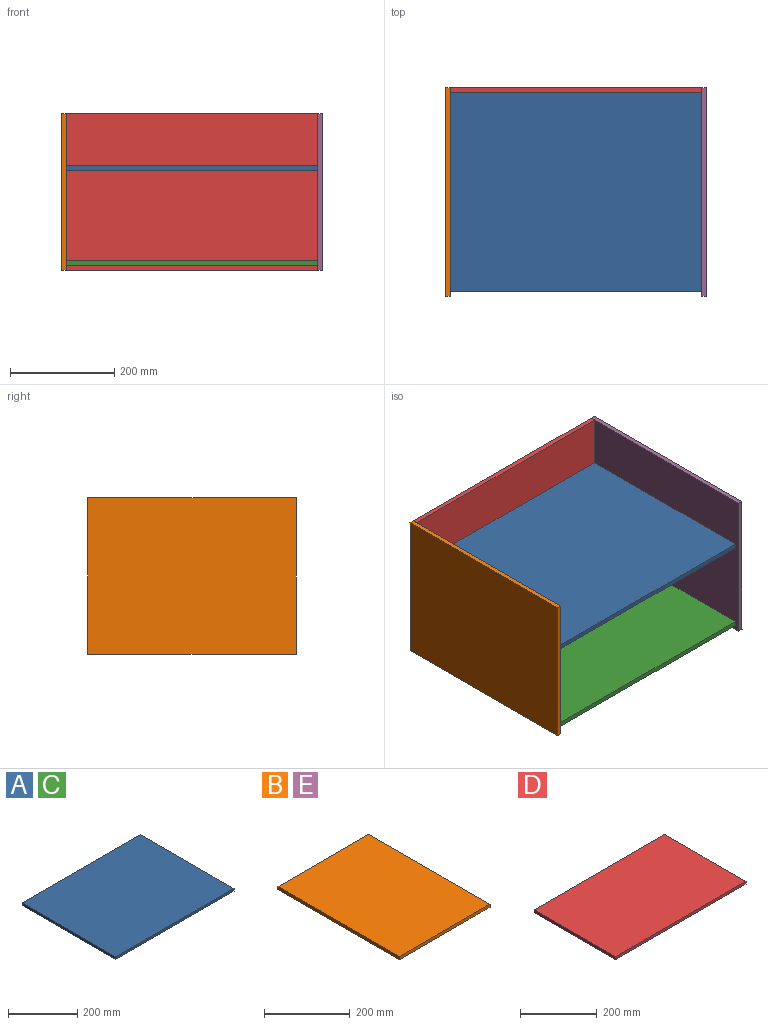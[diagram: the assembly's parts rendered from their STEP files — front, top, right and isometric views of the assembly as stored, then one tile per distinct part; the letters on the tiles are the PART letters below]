
ASSEMBLY  parts=5 mates=4
PART A: 6 faces, bbox 482x382x9 mm
  f0: plane 382x9mm, normal (-1,0,0), area 3438mm2, adj f1,f3,f4,f5
  f1: plane 482x9mm, normal (0,-1,0), area 4338mm2, adj f0,f2,f4,f5
  f2: plane 382x9mm, normal (1,0,0), area 3438mm2, adj f1,f3,f4,f5
  f3: plane 482x9mm, normal (0,1,0), area 4338mm2, adj f0,f2,f4,f5
  f4: plane 482x382mm, normal (0,0,1), area 184124mm2, adj f0,f1,f2,f3
  f5: plane 482x382mm, normal (0,0,-1), area 184124mm2, adj f0,f1,f2,f3
PART B: 6 faces, bbox 300x400x9 mm
  f0: plane 300x9mm, normal (0,-1,0), area 2700mm2, adj f1,f3,f4,f5
  f1: plane 400x9mm, normal (1,0,0), area 3600mm2, adj f0,f2,f4,f5
  f2: plane 300x9mm, normal (0,1,0), area 2700mm2, adj f1,f3,f4,f5
  f3: plane 400x9mm, normal (-1,0,0), area 3600mm2, adj f0,f2,f4,f5
  f4: plane 400x300mm, normal (0,0,1), area 120000mm2, adj f0,f1,f2,f3
  f5: plane 400x300mm, normal (0,0,-1), area 120000mm2, adj f0,f1,f2,f3
PART C: same geometry as A
PART D: 6 faces, bbox 482x300x9 mm
  f0: plane 482x9mm, normal (0,1,0), area 4338mm2, adj f1,f3,f4,f5
  f1: plane 300x9mm, normal (-1,0,0), area 2700mm2, adj f0,f2,f4,f5
  f2: plane 482x9mm, normal (0,-1,0), area 4338mm2, adj f1,f3,f4,f5
  f3: plane 300x9mm, normal (1,0,0), area 2700mm2, adj f0,f2,f4,f5
  f4: plane 482x300mm, normal (0,0,1), area 144600mm2, adj f0,f1,f2,f3
  f5: plane 482x300mm, normal (0,0,-1), area 144600mm2, adj f0,f1,f2,f3
PART E: same geometry as B
PLACE A rot(axis=(-0.99,-0.14,0.04),0deg) t=(-576.22,437.86,-49.01)mm
PLACE B rot(axis=(0,-1,0),90deg) t=(-576.22,428.86,259.99)mm
PLACE C rot(axis=(-0.99,-0.14,0.04),0deg) t=(-576.22,437.86,-231.01)mm
PLACE D rot(axis=(1,0,0),90deg) t=(-576.22,828.86,259.99)mm
PLACE E rot(axis=(0,-1,0),90deg) t=(-85.22,428.86,259.99)mm
MATE fastened E.f4 <-> D.f3  axis (-1,0,0) through (-94.22,828.86,-240.01)mm
MATE fastened D.f1 <-> B.f5  axis (-1,0,0) through (-576.22,828.86,-240.01)mm
MATE fastened A.f0 <-> B.f5  axis (-1,0,0) through (-576.22,628.86,-40.01)mm
MATE fastened C.f0 <-> B.f5  axis (-1,0,0) through (-576.22,628.86,-231.01)mm
